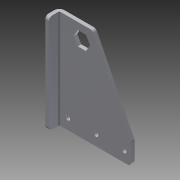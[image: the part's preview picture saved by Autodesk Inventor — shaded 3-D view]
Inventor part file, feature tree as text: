
AUTODESK INVENTOR PART (.ipt)
format: ipt  version: 2014 (Build 180170000, 170)  size: 165,376 bytes
history: native  units: in
note: dims shown in document units (in); Inventor stores cm internally (conversion verified against a paired STEP export)
features: sheet_metal_op x4, other x3, sketch x2, fillet x1
ambient origin geometry x8: Origin, YZ Plane, XZ Plane, XY Plane, X Axis, Y Axis, Z Axis, Center Point
bodies: Solid1 (feature_tree)
feature tree (10):
  sheet_metal_op  "Face1"
  sheet_metal_op  "Flange2"
  fillet  "Fillet1"  Radius=0.125in
  sketch  "Sketch1"  dims[d5=2.5in d6=0.163in d7=0.25in d8=0.375in d11=0.125in]
  other  "Plate1"
  sketch  "Sketch3"  dims[d22=1.1811in d24=1.0in d25=0.3937in d27=1.0in d29=3.5in d30=0.75in d31=1.125in d32=0.5in d34=0.75in d35=0.5in d36=0.125in d37=0.0625in d38=0.25in d39=0.125in d40=0.5in d41=90.0deg d42=0.05in d43=0.5in d44=0.125in d45=0.125in d46=0.125in]
  other  "Plate3"
  sheet_metal_op  "Bend2"
  sheet_metal_op  "Corner2"
  other  "Definition1"
